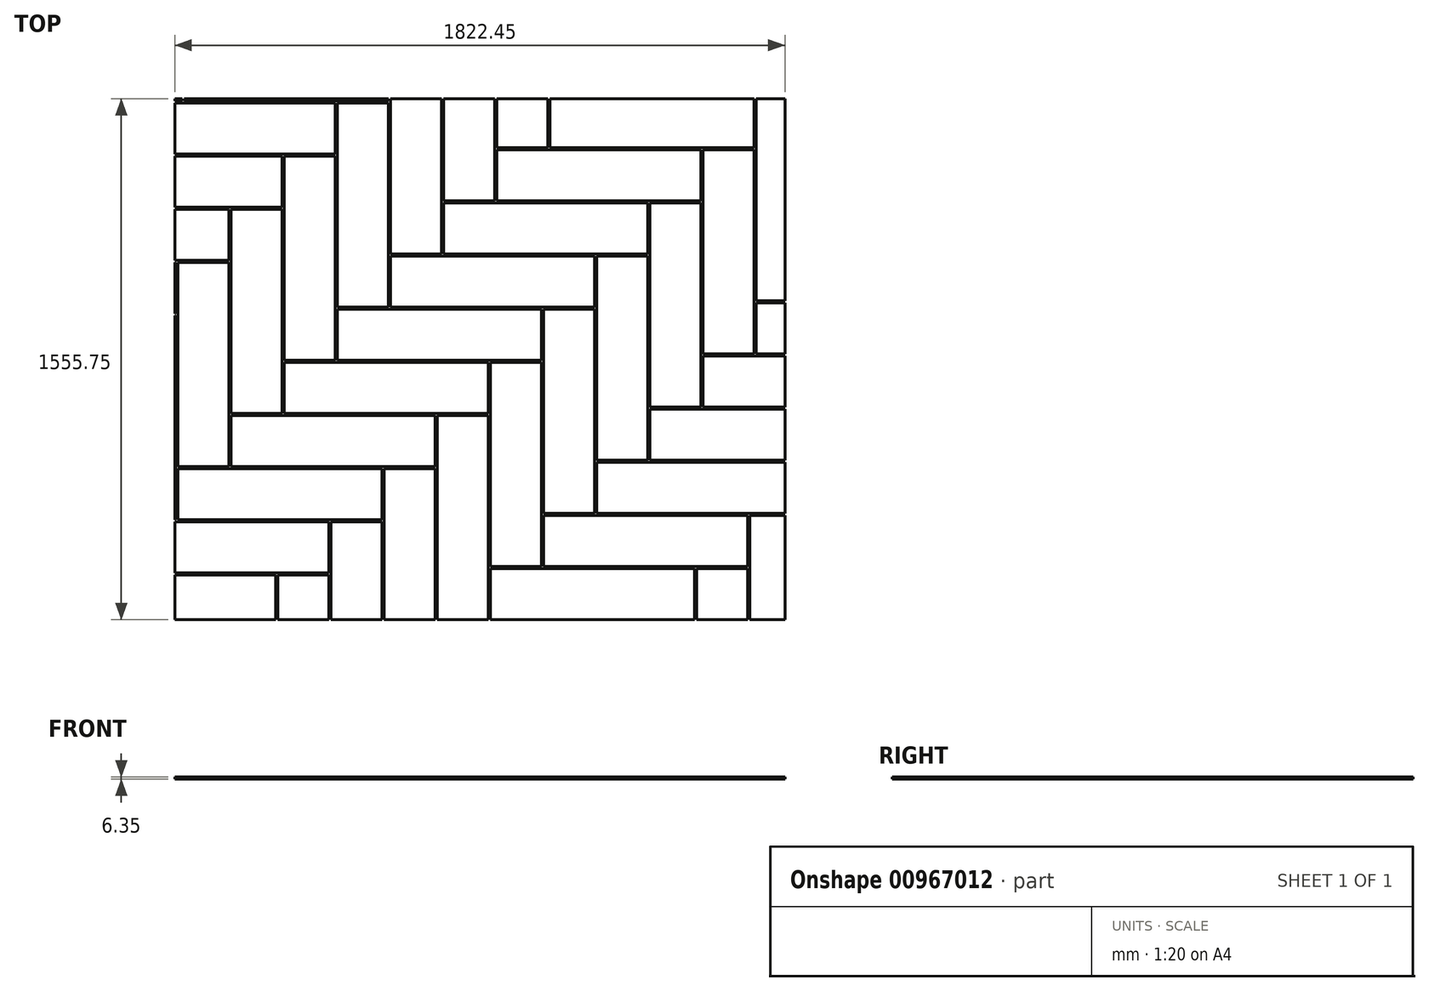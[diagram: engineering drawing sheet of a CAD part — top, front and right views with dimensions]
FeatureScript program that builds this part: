
annotation { "Feature Type Name" : "Feature", "Feature Type Description" : "" }
export const myFeature = defineFeature(function(context is Context, id is Id, definition is map)
    precondition{}
    {
        {
            var Q0;
            Q0=qCreatedBy(makeId("Top.planeOp"),FACE);
            var sketch = newSketch(context, id + "F0", { "sketchPlane" : qUnion([Q0])});
            skLineSegment(sketch, "E0", {"start": v(0, 2298.7) * mm, "end": v(0, 0) * mm});
            skLineSegment(sketch, "E1", {"start": v(0, 0) * mm, "end": v(1822.45, 0) * mm});
            skLineSegment(sketch, "E2", {"start": v(1822.45, 0) * mm, "end": v(1822.45, 1555.75) * mm});
            skLineSegment(sketch, "E3", {"start": v(1822.45, 1555.75) * mm, "end": v(1454.15, 1555.75) * mm});
            skLineSegment(sketch, "E4", {"start": v(1454.15, 1555.75) * mm, "end": v(1454.15, 2298.7) * mm});
            skLineSegment(sketch, "E5", {"start": v(1454.15, 2298.7) * mm, "end": v(0, 2298.7) * mm});
            skSolve(sketch);
        }
        {
            var Q0;
            Q0=qCreatedBy(makeId("Top.planeOp"),FACE);
            var sketch = newSketch(context, id + "F1", { "sketchPlane" : qUnion([Q0])});
            skLineSegment(sketch, "E6", {"start": v(863.6, 0) * mm, "end": v(863.6, -353.23) * mm, "construction": true});
            skLineSegment(sketch, "E7", {"start": v(1631.95, 0) * mm, "end": v(1631.95, -340.06) * mm, "construction": true});
            skLineSegment(sketch, "E8.bottom", {"start": v(942.32, 0) * mm, "end": v(1551.92, 0) * mm});
            skLineSegment(sketch, "E8.top", {"start": v(942.32, 152.4) * mm, "end": v(1551.92, 152.4) * mm});
            skLineSegment(sketch, "E8.left", {"start": v(942.32, 0) * mm, "end": v(942.32, 152.4) * mm});
            skLineSegment(sketch, "E8.right", {"start": v(1551.92, 0) * mm, "end": v(1551.92, 152.4) * mm});
            skLineSegment(sketch, "E9.bottom", {"start": v(942.32, 158.75) * mm, "end": v(1094.72, 158.75) * mm});
            skLineSegment(sketch, "E9.top", {"start": v(942.32, 768.35) * mm, "end": v(1094.72, 768.35) * mm});
            skLineSegment(sketch, "E9.left", {"start": v(942.32, 158.75) * mm, "end": v(942.32, 768.35) * mm});
            skLineSegment(sketch, "E9.right", {"start": v(1094.72, 158.75) * mm, "end": v(1094.72, 768.35) * mm});
            skLineSegment(sketch, "E10.bottom", {"start": v(1101.07, 158.75) * mm, "end": v(1710.67, 158.75) * mm});
            skLineSegment(sketch, "E10.top", {"start": v(1101.07, 311.15) * mm, "end": v(1710.67, 311.15) * mm});
            skLineSegment(sketch, "E10.left", {"start": v(1101.07, 158.75) * mm, "end": v(1101.07, 311.15) * mm});
            skLineSegment(sketch, "E10.right", {"start": v(1710.67, 158.75) * mm, "end": v(1710.67, 311.15) * mm});
            skLineSegment(sketch, "E11.bottom", {"start": v(1101.07, 317.5) * mm, "end": v(1253.47, 317.5) * mm});
            skLineSegment(sketch, "E11.top", {"start": v(1101.07, 927.1) * mm, "end": v(1253.47, 927.1) * mm});
            skLineSegment(sketch, "E11.left", {"start": v(1101.07, 317.5) * mm, "end": v(1101.07, 927.1) * mm});
            skLineSegment(sketch, "E11.right", {"start": v(1253.47, 317.5) * mm, "end": v(1253.47, 927.1) * mm});
            skLineSegment(sketch, "E12.bottom", {"start": v(935.97, 0) * mm, "end": v(783.57, 0) * mm});
            skLineSegment(sketch, "E12.top", {"start": v(935.97, 609.6) * mm, "end": v(783.57, 609.6) * mm});
            skLineSegment(sketch, "E12.left", {"start": v(935.97, 0) * mm, "end": v(935.97, 609.6) * mm});
            skLineSegment(sketch, "E12.right", {"start": v(783.57, 0) * mm, "end": v(783.57, 609.6) * mm});
            skLineSegment(sketch, "E13.bottom", {"start": v(777.22, 609.6) * mm, "end": v(167.62, 609.6) * mm});
            skLineSegment(sketch, "E13.top", {"start": v(777.22, 457.2) * mm, "end": v(167.62, 457.2) * mm});
            skLineSegment(sketch, "E13.left", {"start": v(777.22, 609.6) * mm, "end": v(777.22, 457.2) * mm});
            skLineSegment(sketch, "E13.right", {"start": v(167.62, 609.6) * mm, "end": v(167.62, 457.2) * mm});
            skLineSegment(sketch, "E14.bottom", {"start": v(777.22, 450.85) * mm, "end": v(624.82, 450.85) * mm});
            skLineSegment(sketch, "E14.top", {"start": v(777.22, -158.75) * mm, "end": v(624.82, -158.75) * mm});
            skLineSegment(sketch, "E14.left", {"start": v(777.22, 450.85) * mm, "end": v(777.22, -158.75) * mm});
            skLineSegment(sketch, "E14.right", {"start": v(624.82, 450.85) * mm, "end": v(624.82, -158.75) * mm});
            skLineSegment(sketch, "E15.bottom", {"start": v(618.47, 450.85) * mm, "end": v(8.87, 450.85) * mm});
            skLineSegment(sketch, "E15.top", {"start": v(618.47, 298.45) * mm, "end": v(8.87, 298.45) * mm});
            skLineSegment(sketch, "E15.left", {"start": v(618.47, 450.85) * mm, "end": v(618.47, 298.45) * mm});
            skLineSegment(sketch, "E15.right", {"start": v(8.87, 450.85) * mm, "end": v(8.87, 298.45) * mm});
            skLineSegment(sketch, "E16.bottom", {"start": v(466.07, 292.1) * mm, "end": v(618.47, 292.1) * mm});
            skLineSegment(sketch, "E16.top", {"start": v(466.07, -317.5) * mm, "end": v(618.47, -317.5) * mm});
            skLineSegment(sketch, "E16.left", {"start": v(466.07, 292.1) * mm, "end": v(466.07, -317.5) * mm});
            skLineSegment(sketch, "E16.right", {"start": v(618.47, 292.1) * mm, "end": v(618.47, -317.5) * mm});
            skLineSegment(sketch, "E17.bottom", {"start": v(459.72, 292.1) * mm, "end": v(-149.88, 292.1) * mm});
            skLineSegment(sketch, "E17.top", {"start": v(459.72, 139.7) * mm, "end": v(-149.88, 139.7) * mm});
            skLineSegment(sketch, "E17.left", {"start": v(459.72, 292.1) * mm, "end": v(459.72, 139.7) * mm});
            skLineSegment(sketch, "E17.right", {"start": v(-149.88, 292.1) * mm, "end": v(-149.88, 139.7) * mm});
            skLineSegment(sketch, "E18.bottom", {"start": v(459.72, 133.35) * mm, "end": v(307.32, 133.35) * mm});
            skLineSegment(sketch, "E18.top", {"start": v(459.72, -476.25) * mm, "end": v(307.32, -476.25) * mm});
            skLineSegment(sketch, "E18.left", {"start": v(459.72, 133.35) * mm, "end": v(459.72, -476.25) * mm});
            skLineSegment(sketch, "E18.right", {"start": v(307.32, 133.35) * mm, "end": v(307.32, -476.25) * mm});
            skLineSegment(sketch, "E19.bottom", {"start": v(300.97, -25.4) * mm, "end": v(148.57, -25.4) * mm});
            skLineSegment(sketch, "E19.top", {"start": v(300.97, -635) * mm, "end": v(148.57, -635) * mm});
            skLineSegment(sketch, "E19.left", {"start": v(300.97, -25.4) * mm, "end": v(300.97, -635) * mm});
            skLineSegment(sketch, "E19.right", {"start": v(148.57, -25.4) * mm, "end": v(148.57, -635) * mm});
            skLineSegment(sketch, "E20.bottom", {"start": v(300.97, 133.35) * mm, "end": v(-308.63, 133.35) * mm});
            skLineSegment(sketch, "E20.top", {"start": v(300.97, -19.05) * mm, "end": v(-308.63, -19.05) * mm});
            skLineSegment(sketch, "E20.left", {"start": v(300.97, 133.35) * mm, "end": v(300.97, -19.05) * mm});
            skLineSegment(sketch, "E20.right", {"start": v(-308.63, 133.35) * mm, "end": v(-308.63, -19.05) * mm});
            skLineSegment(sketch, "E21.bottom", {"start": v(935.97, 615.95) * mm, "end": v(326.37, 615.95) * mm});
            skLineSegment(sketch, "E21.top", {"start": v(935.97, 768.35) * mm, "end": v(326.37, 768.35) * mm});
            skLineSegment(sketch, "E21.left", {"start": v(935.97, 615.95) * mm, "end": v(935.97, 768.35) * mm});
            skLineSegment(sketch, "E21.right", {"start": v(326.37, 615.95) * mm, "end": v(326.37, 768.35) * mm});
            skLineSegment(sketch, "E22.bottom", {"start": v(1094.72, 774.7) * mm, "end": v(485.12, 774.7) * mm});
            skLineSegment(sketch, "E22.top", {"start": v(1094.72, 927.1) * mm, "end": v(485.12, 927.1) * mm});
            skLineSegment(sketch, "E22.left", {"start": v(1094.72, 774.7) * mm, "end": v(1094.72, 927.1) * mm});
            skLineSegment(sketch, "E22.right", {"start": v(485.12, 774.7) * mm, "end": v(485.12, 927.1) * mm});
            skLineSegment(sketch, "E23.bottom", {"start": v(1253.47, 933.45) * mm, "end": v(643.87, 933.45) * mm});
            skLineSegment(sketch, "E23.top", {"start": v(1253.47, 1085.85) * mm, "end": v(643.87, 1085.85) * mm});
            skLineSegment(sketch, "E23.left", {"start": v(1253.47, 933.45) * mm, "end": v(1253.47, 1085.85) * mm});
            skLineSegment(sketch, "E23.right", {"start": v(643.87, 933.45) * mm, "end": v(643.87, 1085.85) * mm});
            skLineSegment(sketch, "E24.bottom", {"start": v(1259.82, 317.5) * mm, "end": v(1869.42, 317.5) * mm});
            skLineSegment(sketch, "E24.top", {"start": v(1259.82, 469.9) * mm, "end": v(1869.42, 469.9) * mm});
            skLineSegment(sketch, "E24.left", {"start": v(1259.82, 317.5) * mm, "end": v(1259.82, 469.9) * mm});
            skLineSegment(sketch, "E24.right", {"start": v(1869.42, 317.5) * mm, "end": v(1869.42, 469.9) * mm});
            skLineSegment(sketch, "E25.bottom", {"start": v(1259.82, 476.25) * mm, "end": v(1412.22, 476.25) * mm});
            skLineSegment(sketch, "E25.top", {"start": v(1259.82, 1085.85) * mm, "end": v(1412.22, 1085.85) * mm});
            skLineSegment(sketch, "E25.left", {"start": v(1259.82, 476.25) * mm, "end": v(1259.82, 1085.85) * mm});
            skLineSegment(sketch, "E25.right", {"start": v(1412.22, 476.25) * mm, "end": v(1412.22, 1085.85) * mm});
            skLineSegment(sketch, "E26.bottom", {"start": v(1418.57, 476.25) * mm, "end": v(2028.17, 476.25) * mm});
            skLineSegment(sketch, "E26.top", {"start": v(1418.57, 628.65) * mm, "end": v(2028.17, 628.65) * mm});
            skLineSegment(sketch, "E26.left", {"start": v(1418.57, 476.25) * mm, "end": v(1418.57, 628.65) * mm});
            skLineSegment(sketch, "E26.right", {"start": v(2028.17, 476.25) * mm, "end": v(2028.17, 628.65) * mm});
            skLineSegment(sketch, "E27.bottom", {"start": v(1418.57, 635) * mm, "end": v(1570.97, 635) * mm});
            skLineSegment(sketch, "E27.top", {"start": v(1418.57, 1244.6) * mm, "end": v(1570.97, 1244.6) * mm});
            skLineSegment(sketch, "E27.left", {"start": v(1418.57, 635) * mm, "end": v(1418.57, 1244.6) * mm});
            skLineSegment(sketch, "E27.right", {"start": v(1570.97, 635) * mm, "end": v(1570.97, 1244.6) * mm});
            skLineSegment(sketch, "E28.bottom", {"start": v(1577.32, 635) * mm, "end": v(2186.92, 635) * mm});
            skLineSegment(sketch, "E28.top", {"start": v(1577.32, 787.4) * mm, "end": v(2186.92, 787.4) * mm});
            skLineSegment(sketch, "E28.left", {"start": v(1577.32, 635) * mm, "end": v(1577.32, 787.4) * mm});
            skLineSegment(sketch, "E28.right", {"start": v(2186.92, 635) * mm, "end": v(2186.92, 787.4) * mm});
            skLineSegment(sketch, "E29.bottom", {"start": v(1412.22, 1244.6) * mm, "end": v(802.62, 1244.6) * mm});
            skLineSegment(sketch, "E29.top", {"start": v(1412.22, 1092.2) * mm, "end": v(802.62, 1092.2) * mm});
            skLineSegment(sketch, "E29.left", {"start": v(1412.22, 1244.6) * mm, "end": v(1412.22, 1092.2) * mm});
            skLineSegment(sketch, "E29.right", {"start": v(802.62, 1244.6) * mm, "end": v(802.62, 1092.2) * mm});
            skLineSegment(sketch, "E30.bottom", {"start": v(1577.32, 793.75) * mm, "end": v(1729.72, 793.75) * mm});
            skLineSegment(sketch, "E30.top", {"start": v(1577.32, 1403.35) * mm, "end": v(1729.72, 1403.35) * mm});
            skLineSegment(sketch, "E30.left", {"start": v(1577.32, 793.75) * mm, "end": v(1577.32, 1403.35) * mm});
            skLineSegment(sketch, "E30.right", {"start": v(1729.72, 793.75) * mm, "end": v(1729.72, 1403.35) * mm});
            skLineSegment(sketch, "E31.bottom", {"start": v(1736.07, 793.75) * mm, "end": v(2345.67, 793.75) * mm});
            skLineSegment(sketch, "E31.top", {"start": v(1736.07, 946.15) * mm, "end": v(2345.67, 946.15) * mm});
            skLineSegment(sketch, "E31.left", {"start": v(1736.07, 793.75) * mm, "end": v(1736.07, 946.15) * mm});
            skLineSegment(sketch, "E31.right", {"start": v(2345.67, 793.75) * mm, "end": v(2345.67, 946.15) * mm});
            skLineSegment(sketch, "E32.bottom", {"start": v(1570.97, 1403.35) * mm, "end": v(961.37, 1403.35) * mm});
            skLineSegment(sketch, "E32.top", {"start": v(1570.97, 1250.95) * mm, "end": v(961.37, 1250.95) * mm});
            skLineSegment(sketch, "E32.left", {"start": v(1570.97, 1403.35) * mm, "end": v(1570.97, 1250.95) * mm});
            skLineSegment(sketch, "E32.right", {"start": v(961.37, 1403.35) * mm, "end": v(961.37, 1250.95) * mm});
            skLineSegment(sketch, "E33.bottom", {"start": v(802.62, 1250.95) * mm, "end": v(955.02, 1250.95) * mm});
            skLineSegment(sketch, "E33.top", {"start": v(802.62, 1860.55) * mm, "end": v(955.02, 1860.55) * mm});
            skLineSegment(sketch, "E33.left", {"start": v(802.62, 1250.95) * mm, "end": v(802.62, 1860.55) * mm});
            skLineSegment(sketch, "E33.right", {"start": v(955.02, 1250.95) * mm, "end": v(955.02, 1860.55) * mm});
            skLineSegment(sketch, "E34.bottom", {"start": v(796.27, 1092.2) * mm, "end": v(643.87, 1092.2) * mm});
            skLineSegment(sketch, "E34.top", {"start": v(796.27, 1701.8) * mm, "end": v(643.87, 1701.8) * mm});
            skLineSegment(sketch, "E34.left", {"start": v(796.27, 1092.2) * mm, "end": v(796.27, 1701.8) * mm});
            skLineSegment(sketch, "E34.right", {"start": v(643.87, 1092.2) * mm, "end": v(643.87, 1701.8) * mm});
            skLineSegment(sketch, "E35.bottom", {"start": v(637.52, 933.45) * mm, "end": v(485.12, 933.45) * mm});
            skLineSegment(sketch, "E35.top", {"start": v(637.52, 1543.05) * mm, "end": v(485.12, 1543.05) * mm});
            skLineSegment(sketch, "E35.left", {"start": v(637.52, 933.45) * mm, "end": v(637.52, 1543.05) * mm});
            skLineSegment(sketch, "E35.right", {"start": v(485.12, 933.45) * mm, "end": v(485.12, 1543.05) * mm});
            skLineSegment(sketch, "E36.bottom", {"start": v(478.77, 774.7) * mm, "end": v(326.37, 774.7) * mm});
            skLineSegment(sketch, "E36.top", {"start": v(478.77, 1384.3) * mm, "end": v(326.37, 1384.3) * mm});
            skLineSegment(sketch, "E36.left", {"start": v(478.77, 774.7) * mm, "end": v(478.77, 1384.3) * mm});
            skLineSegment(sketch, "E36.right", {"start": v(326.37, 774.7) * mm, "end": v(326.37, 1384.3) * mm});
            skLineSegment(sketch, "E37.bottom", {"start": v(320.02, 615.95) * mm, "end": v(167.62, 615.95) * mm});
            skLineSegment(sketch, "E37.top", {"start": v(320.02, 1225.55) * mm, "end": v(167.62, 1225.55) * mm});
            skLineSegment(sketch, "E37.left", {"start": v(320.02, 615.95) * mm, "end": v(320.02, 1225.55) * mm});
            skLineSegment(sketch, "E37.right", {"start": v(167.62, 615.95) * mm, "end": v(167.62, 1225.55) * mm});
            skLineSegment(sketch, "E38.bottom", {"start": v(161.27, 457.2) * mm, "end": v(8.87, 457.2) * mm});
            skLineSegment(sketch, "E38.top", {"start": v(161.27, 1066.8) * mm, "end": v(8.87, 1066.8) * mm});
            skLineSegment(sketch, "E38.left", {"start": v(161.27, 457.2) * mm, "end": v(161.27, 1066.8) * mm});
            skLineSegment(sketch, "E38.right", {"start": v(8.87, 457.2) * mm, "end": v(8.87, 1066.8) * mm});
            skLineSegment(sketch, "E39.bottom", {"start": v(1558.27, 152.4) * mm, "end": v(1710.67, 152.4) * mm});
            skLineSegment(sketch, "E39.top", {"start": v(1558.27, -457.2) * mm, "end": v(1710.67, -457.2) * mm});
            skLineSegment(sketch, "E39.left", {"start": v(1558.27, 152.4) * mm, "end": v(1558.27, -457.2) * mm});
            skLineSegment(sketch, "E39.right", {"start": v(1710.67, 152.4) * mm, "end": v(1710.67, -457.2) * mm});
            skLineSegment(sketch, "E40.bottom", {"start": v(1717.02, 311.15) * mm, "end": v(1869.42, 311.15) * mm});
            skLineSegment(sketch, "E40.top", {"start": v(1717.02, -298.45) * mm, "end": v(1869.42, -298.45) * mm});
            skLineSegment(sketch, "E40.left", {"start": v(1717.02, 311.15) * mm, "end": v(1717.02, -298.45) * mm});
            skLineSegment(sketch, "E40.right", {"start": v(1869.42, 311.15) * mm, "end": v(1869.42, -298.45) * mm});
            skLineSegment(sketch, "E41.bottom", {"start": v(1875.77, 469.9) * mm, "end": v(2028.17, 469.9) * mm});
            skLineSegment(sketch, "E41.top", {"start": v(1875.77, -139.7) * mm, "end": v(2028.17, -139.7) * mm});
            skLineSegment(sketch, "E41.left", {"start": v(1875.77, 469.9) * mm, "end": v(1875.77, -139.7) * mm});
            skLineSegment(sketch, "E41.right", {"start": v(2028.17, 469.9) * mm, "end": v(2028.17, -139.7) * mm});
            skLineSegment(sketch, "E42.bottom", {"start": v(2.52, 298.45) * mm, "end": v(-149.88, 298.45) * mm});
            skLineSegment(sketch, "E42.top", {"start": v(2.52, 908.05) * mm, "end": v(-149.88, 908.05) * mm});
            skLineSegment(sketch, "E42.left", {"start": v(2.52, 298.45) * mm, "end": v(2.52, 908.05) * mm});
            skLineSegment(sketch, "E42.right", {"start": v(-149.88, 298.45) * mm, "end": v(-149.88, 908.05) * mm});
            skLineSegment(sketch, "E43.bottom", {"start": v(961.37, 1409.7) * mm, "end": v(1113.77, 1409.7) * mm});
            skLineSegment(sketch, "E43.top", {"start": v(961.37, 2019.3) * mm, "end": v(1113.77, 2019.3) * mm});
            skLineSegment(sketch, "E43.left", {"start": v(961.37, 1409.7) * mm, "end": v(961.37, 2019.3) * mm});
            skLineSegment(sketch, "E43.right", {"start": v(1113.77, 1409.7) * mm, "end": v(1113.77, 2019.3) * mm});
            skLineSegment(sketch, "E44.bottom", {"start": v(1120.12, 1409.7) * mm, "end": v(1729.72, 1409.7) * mm});
            skLineSegment(sketch, "E44.top", {"start": v(1120.12, 1562.1) * mm, "end": v(1729.72, 1562.1) * mm});
            skLineSegment(sketch, "E44.left", {"start": v(1120.12, 1409.7) * mm, "end": v(1120.12, 1562.1) * mm});
            skLineSegment(sketch, "E44.right", {"start": v(1729.72, 1409.7) * mm, "end": v(1729.72, 1562.1) * mm});
            skLineSegment(sketch, "E45.bottom", {"start": v(-156.23, 139.7) * mm, "end": v(-308.63, 139.7) * mm});
            skLineSegment(sketch, "E45.top", {"start": v(-156.23, 749.3) * mm, "end": v(-308.63, 749.3) * mm});
            skLineSegment(sketch, "E45.left", {"start": v(-156.23, 139.7) * mm, "end": v(-156.23, 749.3) * mm});
            skLineSegment(sketch, "E45.right", {"start": v(-308.63, 139.7) * mm, "end": v(-308.63, 749.3) * mm});
            skLineSegment(sketch, "E46.bottom", {"start": v(-156.23, 908.05) * mm, "end": v(-765.83, 908.05) * mm});
            skLineSegment(sketch, "E46.top", {"start": v(-156.23, 755.65) * mm, "end": v(-765.83, 755.65) * mm});
            skLineSegment(sketch, "E46.left", {"start": v(-156.23, 908.05) * mm, "end": v(-156.23, 755.65) * mm});
            skLineSegment(sketch, "E46.right", {"start": v(-765.83, 908.05) * mm, "end": v(-765.83, 755.65) * mm});
            skLineSegment(sketch, "E47.bottom", {"start": v(2.52, 1066.8) * mm, "end": v(-607.08, 1066.8) * mm});
            skLineSegment(sketch, "E47.top", {"start": v(2.52, 914.4) * mm, "end": v(-607.08, 914.4) * mm});
            skLineSegment(sketch, "E47.left", {"start": v(2.52, 1066.8) * mm, "end": v(2.52, 914.4) * mm});
            skLineSegment(sketch, "E47.right", {"start": v(-607.08, 1066.8) * mm, "end": v(-607.08, 914.4) * mm});
            skLineSegment(sketch, "E48.bottom", {"start": v(161.27, 1225.55) * mm, "end": v(-448.33, 1225.55) * mm});
            skLineSegment(sketch, "E48.top", {"start": v(161.27, 1073.15) * mm, "end": v(-448.33, 1073.15) * mm});
            skLineSegment(sketch, "E48.left", {"start": v(161.27, 1225.55) * mm, "end": v(161.27, 1073.15) * mm});
            skLineSegment(sketch, "E48.right", {"start": v(-448.33, 1225.55) * mm, "end": v(-448.33, 1073.15) * mm});
            skLineSegment(sketch, "E49.bottom", {"start": v(320.02, 1384.3) * mm, "end": v(-289.58, 1384.3) * mm});
            skLineSegment(sketch, "E49.top", {"start": v(320.02, 1231.9) * mm, "end": v(-289.58, 1231.9) * mm});
            skLineSegment(sketch, "E49.left", {"start": v(320.02, 1384.3) * mm, "end": v(320.02, 1231.9) * mm});
            skLineSegment(sketch, "E49.right", {"start": v(-289.58, 1384.3) * mm, "end": v(-289.58, 1231.9) * mm});
            skLineSegment(sketch, "E50.bottom", {"start": v(478.77, 1543.05) * mm, "end": v(-130.83, 1543.05) * mm});
            skLineSegment(sketch, "E50.top", {"start": v(478.77, 1390.65) * mm, "end": v(-130.83, 1390.65) * mm});
            skLineSegment(sketch, "E50.left", {"start": v(478.77, 1543.05) * mm, "end": v(478.77, 1390.65) * mm});
            skLineSegment(sketch, "E50.right", {"start": v(-130.83, 1543.05) * mm, "end": v(-130.83, 1390.65) * mm});
            skLineSegment(sketch, "E51.bottom", {"start": v(637.52, 1701.8) * mm, "end": v(27.92, 1701.8) * mm});
            skLineSegment(sketch, "E51.top", {"start": v(637.52, 1549.4) * mm, "end": v(27.92, 1549.4) * mm});
            skLineSegment(sketch, "E51.left", {"start": v(637.52, 1701.8) * mm, "end": v(637.52, 1549.4) * mm});
            skLineSegment(sketch, "E51.right", {"start": v(27.92, 1701.8) * mm, "end": v(27.92, 1549.4) * mm});
            skLineSegment(sketch, "E52.bottom", {"start": v(21.57, 1549.4) * mm, "end": v(-130.83, 1549.4) * mm});
            skLineSegment(sketch, "E52.top", {"start": v(21.57, 2159) * mm, "end": v(-130.83, 2159) * mm});
            skLineSegment(sketch, "E52.left", {"start": v(21.57, 1549.4) * mm, "end": v(21.57, 2159) * mm});
            skLineSegment(sketch, "E52.right", {"start": v(-130.83, 1549.4) * mm, "end": v(-130.83, 2159) * mm});
            skLineSegment(sketch, "E53.bottom", {"start": v(-137.18, 1390.65) * mm, "end": v(-289.58, 1390.65) * mm});
            skLineSegment(sketch, "E53.top", {"start": v(-137.18, 2000.25) * mm, "end": v(-289.58, 2000.25) * mm});
            skLineSegment(sketch, "E53.left", {"start": v(-137.18, 1390.65) * mm, "end": v(-137.18, 2000.25) * mm});
            skLineSegment(sketch, "E53.right", {"start": v(-289.58, 1390.65) * mm, "end": v(-289.58, 2000.25) * mm});
            skLineSegment(sketch, "E54.bottom", {"start": v(1736.07, 952.5) * mm, "end": v(1888.47, 952.5) * mm});
            skLineSegment(sketch, "E54.top", {"start": v(1736.07, 1562.1) * mm, "end": v(1888.47, 1562.1) * mm});
            skLineSegment(sketch, "E54.left", {"start": v(1736.07, 952.5) * mm, "end": v(1736.07, 1562.1) * mm});
            skLineSegment(sketch, "E54.right", {"start": v(1888.47, 952.5) * mm, "end": v(1888.47, 1562.1) * mm});
            skSolve(sketch);
        }
        {
            var Q0;
            Q0 = qSketchRegion(id + "F1", true);
            extrude(context, id + "F2", {"entities" : qUnion([Q0]), "depth" : 6.35 * mm, "offsetDistance" : 25.4 * mm});
        }
        {
            var Q0;
            Q0=qCreatedBy(makeId("Top.planeOp"),FACE);
            var sketch = newSketch(context, id + "F3", { "sketchPlane" : qUnion([Q0])});
            skLineSegment(sketch, "E55.0", {"start": v(0, 1555.75) * mm, "end": v(0, 0) * mm});
            skLineSegment(sketch, "E55.1", {"start": v(0, 0) * mm, "end": v(1822.45, 0) * mm});
            skLineSegment(sketch, "E55.2", {"start": v(1822.45, 0) * mm, "end": v(1822.45, 1555.75) * mm});
            skLineSegment(sketch, "E55.3", {"start": v(1822.45, 1555.75) * mm, "end": v(0, 1555.75) * mm});
            skLineSegment(sketch, "E56.bottom", {"start": v(-1287.42, 2782.55) * mm, "end": v(3002.2, 2782.55) * mm});
            skLineSegment(sketch, "E56.top", {"start": v(-1287.42, -1222.55) * mm, "end": v(3002.2, -1222.55) * mm});
            skLineSegment(sketch, "E56.left", {"start": v(-1287.42, 2782.55) * mm, "end": v(-1287.42, -1222.55) * mm});
            skLineSegment(sketch, "E56.right", {"start": v(3002.2, 2782.55) * mm, "end": v(3002.2, -1222.55) * mm});
            skSolve(sketch);
        }
        {
            var Q0;
            Q0 = qSketchRegion(id + "F3", true);
            extrude(context, id + "F4", {"entities" : qUnion([Q0]), "operationType" : NewBodyOperationType.REMOVE, "endBound" : BoundingType.THROUGH_ALL, "depth" : 25.4 * mm, "offsetDistance" : 25.4 * mm});
        }
    });
